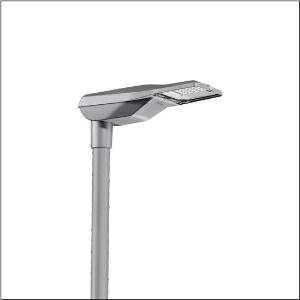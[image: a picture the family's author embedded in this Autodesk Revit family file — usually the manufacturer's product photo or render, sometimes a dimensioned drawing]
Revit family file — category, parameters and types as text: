
# Revit family: streetlight_sl_21_iq_micro___stw1_0a_5xe1e41d08cb_a1a9
name_source: partatom
category: Lighting Fixtures
units: mm (PartAtom-declared; Revit-internal decimal feet)

## family parameters
Cut with Voids When Loaded = No
Host = Face
Light Source = No
Part Type = Normal
Room Calculation Point = No
Round Connector Dimension = Use Diameter
Shared = No

## types (1)
- --- (1 x LED, 2980 lm, 19.4 W, 4000K)
    Apparent Load = 19 VA
    CIE Flux Codes = 38 75 98 100 100
    Color Rendering = 70
    Color Temperature = 4000K
    Default Elevation = 1800 mm
    Description = Streetlight SL 21 iQ micro, mast luminaire, primary light control with lens, of PMMA, primary optical cover: cover, of toughened safety glass, transparent, light distribution: STW1.0a, light emission: direct distribution, primary light characteristic: asymmetric, installation type: post-top, side-entry, LED, High Power LED, rated luminous flux: 2.980lm, luminous efficacy: 154lm/W, light colour: 740, colour temperature: 4000K, control gear: iQ-Comfort, control: Auto-Match, Temp-Guard, Lumen-Switch, Night-Set, Smart-Wire, Light-Fading, Desk-Remote (wireless, voltage-free reading and setting of iQ features in the workshop via application-optimized NFC function/RFID function), optimised constant luminous flux control (CLO 2.0), pre-setting: linear dimming characteristic, mains connection: 220..240V, AC, 50/60Hz, start of lifetime: 19W, end of service life: 20W, reduction: 10W, luminaire housing, of diecast aluminium, powder-coated, Siteco® metallic grey (DB 702S), corrosivity category C5 high according to DIN EN ISO 12944, please order mast flange separately, inclination adjustable: 0°, 5°, 10°, 15°, sealing non-destructively replaceable, multi-level sealing system, length: 528mm, width: 235mm, height: 110mm, mast flange for spigot size: 42mm (side-entry): 5XC10008XM4, 60/48mm (side-entry/post-top): 5XC10108XM2, 76/60mm (side-entry/post-top): 5XC10108XM1, protection rating (complete): IP66, insulation class (complete): insulation class II (safety insulation), certification: CE, ENEC, ENEC+, VDE, impact resistance: IK10, permissible operating ambient temperature for outdoor applications: -40..+50°C, standard-compliant lighting for roads and squares, packaging unit: 1 piece

Light Distribution: STW1.0a
    Height = 110 mm
    Lamp = 1 x LED
    Lamp Light Flux = 2980 lm
    Lamp Power = 19.4 W
    Lamp count = 1
    Length = 528 mm
    Luminous efficacy = 154 lm/W
    Manufacturer = Siteco
    ModVariant = No
    Model = 5XE1E41D08CB
    Number of Poles = 1
    OnlyDefault = Yes
    Power Factor = 1
    Product Name = Streetlight SL 21 iQ micro | STW1.0a
    Product group = mast luminaire | pylon top
    ProductGroupID = 6100
    Protection Class = Protection class II
    Protection Degree = IP 66
    RLX_Detail_Level = 1
    RLX_Emergency_Light_Flux = 0 lm
    RLX_Emergency_Type = 0
    RLX_Emergency_Type_DB = No
    RlxData = <blob elided: 98973 chars, md5=a5c07643>
    Socket = socket
    Standby Power = 0 W
    System Light Flux = 2980 lm
    System Power = 19 W
    Type Comments = factory setting: luminous flux: 100 % | dim-lin: 254 | 387 mA
    Type Image = l_1006881.jpg
    URL = http://relux.com
    VarID = @adj_142101
    Voltage = 0 V
    Weight = 0.00 kg
    Width = 235 mm

## geometry (parser evidence)
native form markers: Blend x4, Sweep x10
no freeform markers — native parametric forms only
